# Revit family: FU_Modular_Sandler_Flow 06063
name_source: partatom
category: Furniture
units: mm (PartAtom-declared; Revit-internal decimal feet)

## family parameters
Always vertical = Yes
Cut with Voids When Loaded = No
OmniClass Number = 23.40.20.00
OmniClass Title = General Furniture and Specialties
Render Appearance Source = Family Geometry
Room Calculation Point = No
Shared = No
Work Plane-Based = No

## types (1)
- Flow 06063
    Default Elevation = 0 mm  [stored 0 ft]
    Depth = 1570 mm  [stored 5.15092 ft]
    Description = Right-hand modular sofa seat in an irregular 'L' shape. The backrest is fixed in a curved position, and the seat is webbed for comfort.
    Height = 450 mm  [stored 1.47638 ft]
    Manufacturer = Sandler
    Model = Flow 06063
    URL = https://www.sandlerseating.com
    Width = 2330 mm  [stored 7.64436 ft]

note: [stored X ft] marks values corroborated as IEEE doubles in the binary element streams (Revit-internal decimal feet)

## geometry (parser evidence)
native form markers: Sweep x6
no freeform markers — native parametric forms only
